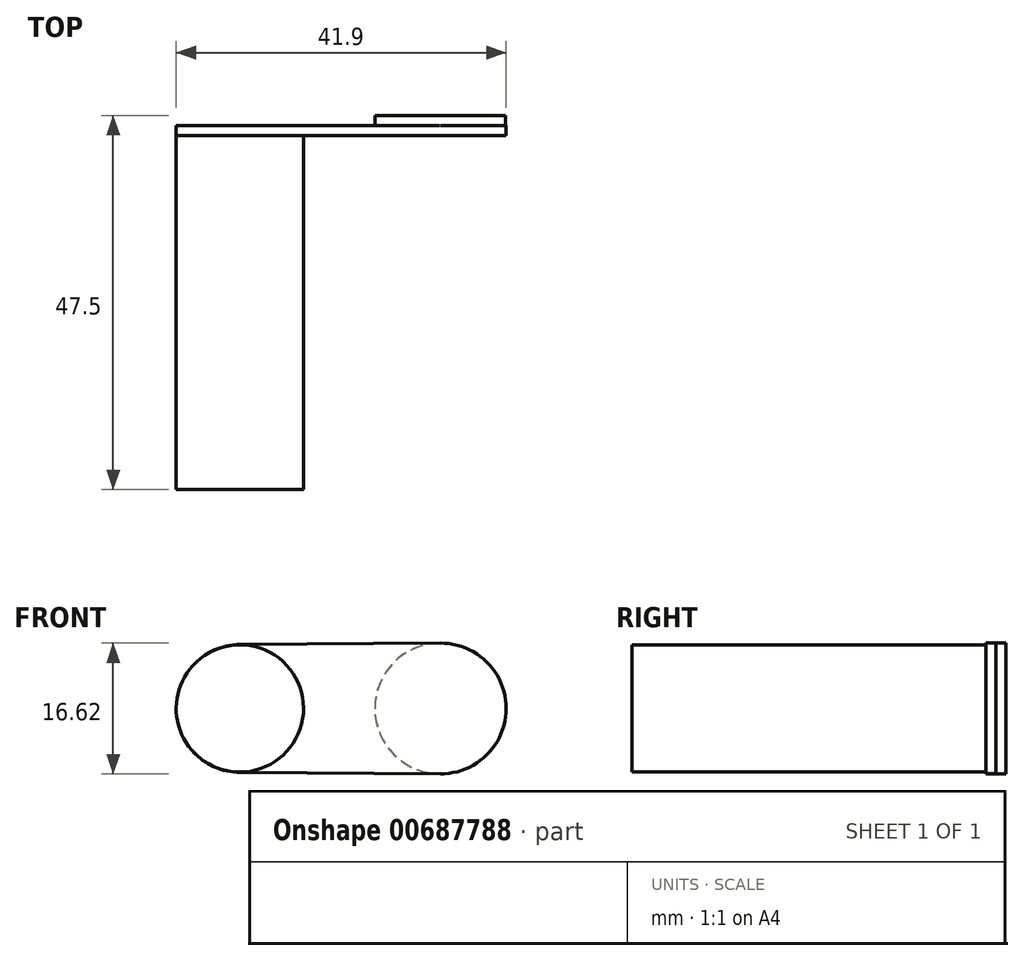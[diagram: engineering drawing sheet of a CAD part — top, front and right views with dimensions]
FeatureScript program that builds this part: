
annotation { "Feature Type Name" : "Feature", "Feature Type Description" : "" }
export const myFeature = defineFeature(function(context is Context, id is Id, definition is map)
    precondition{}
    {
        {
            var Q0;
            Q0=qCreatedBy(makeId("Front.planeOp"),FACE);
            var sketch = newSketch(context, id + "F0", { "sketchPlane" : qUnion([Q0])});
            skCircle(sketch, "E0", {"center": v(0, 0) * mm, "radius": 8.3 * mm});
            skSolve(sketch);
        }
        {
            var Q0;
            Q0=makeQuery(id+"F0.imprint","IMPRINT",FACE,{"disambiguationData":[TD([[makeQuery(id+"F0.imprint","IMPRINT",EDGE,{"derivedFrom":sQuery(id+"F0.wireOp",EDGE,"E0")}),1.0]])]});
            extrude(context, id + "F1", {"entities" : qUnion([Q0]), "depth" : 1.27 * mm, "offsetDistance" : 25.4 * mm});
        }
        {
            var Q0;
            Q0=makeQuery(id+"F1.opExtrude","CAP_FACE",FACE,{"disambiguationData":[OSD([sQuery(id+"F0.wireOp",EDGE,"E0")])],"isStart":false});
            var sketch = newSketch(context, id + "F2", { "sketchPlane" : qUnion([Q0])});
            skPoint(sketch, "E1", {"position": v(-25.4, 0) * mm});
            skArc(sketch, "E2", {"start": v(-25.46, 8.13) * mm, "mid": v(-33.53, -0.03) * mm, "end": v(-25.4, -8.13) * mm});
            skLineSegment(sketch, "E3", {"start": v(-25.4, -8.13) * mm, "end": v(0, -8.3) * mm});
            skLineSegment(sketch, "E4", {"start": v(0, 8.3) * mm, "end": v(-25.46, 8.13) * mm});
            skArc(sketch, "E5", {"start": v(0, -8.3) * mm, "mid": v(8.36, 0) * mm, "end": v(0, 8.3) * mm});
            skSolve(sketch);
        }
        {
            var Q0;
            {var subQ0=sQuery(id+"F2.wireOp",EDGE,"E5");Q0=makeQuery(id+"F2.imprint","IMPRINT",FACE,{"disambiguationData":[TD([[makeQuery(id+"F2.imprint","IMPRINT",EDGE,{"derivedFrom":subQ0}),1.0]])]});}
            var Q1;
            {var subQ0=sQuery(id+"F2.wireOp",EDGE,"E2");Q1=makeQuery(id+"F2.imprint","IMPRINT",FACE,{"disambiguationData":[TD([[makeQuery(id+"F2.imprint","IMPRINT",EDGE,{"derivedFrom":subQ0}),1.0]])]});}
            var Q2;
            {var subQ1=makeQuery(id+"F1.opExtrude","CAP_EDGE",EDGE,{"disambiguationData":[OSD([sQuery(id+"F0.wireOp",EDGE,"E0")])],"isStart":false});var subQ4=makeQuery(id+"F2.imprint","INTERSECT",VERTEX,{"derivedFrom":[subQ1,sQuery(id+"F2.wireOp",EDGE,"E3")]});Q2=makeQuery(id+"F2.imprint","IMPRINT",FACE,{"disambiguationData":[TD([[makeQuery(id+"F2.imprint","IMPRINT",EDGE,{"disambiguationData":[TD([[subQ4,1.0]])],"derivedFrom":subQ1}),1.0]])]});}
            extrude(context, id + "F3", {"entities" : qUnion([Q0, Q1, Q2]), "operationType" : NewBodyOperationType.ADD, "depth" : 1.27 * mm, "offsetDistance" : 25.4 * mm});
        }
        {
            var Q0;
            Q0=makeQuery(id+"F3.opExtrude","CAP_FACE",FACE,{"disambiguationData":[OSD([sQuery(id+"F2.wireOp",EDGE,"E2"),sQuery(id+"F2.wireOp",EDGE,"E3"),sQuery(id+"F2.wireOp",EDGE,"E4"),sQuery(id+"F2.wireOp",EDGE,"E5")])],"isStart":false});
            var sketch = newSketch(context, id + "F4", { "sketchPlane" : qUnion([Q0])});
            skCircle(sketch, "E6", {"center": v(-25.46, 0) * mm, "radius": 8.09 * mm});
            skSolve(sketch);
        }
        {
            var Q0;
            Q0 = qSketchRegion(id + "F4", true);
            extrude(context, id + "F5", {"entities" : qUnion([Q0]), "operationType" : NewBodyOperationType.ADD, "depth" : 44.96 * mm, "offsetDistance" : 25.4 * mm});
        }
    });
